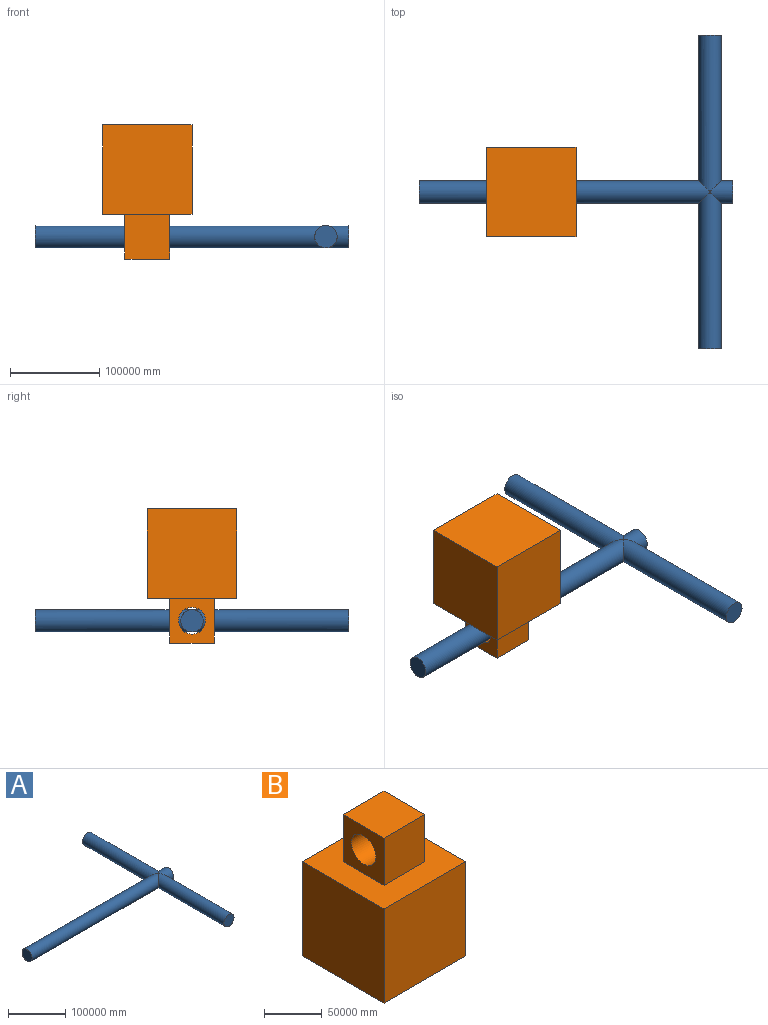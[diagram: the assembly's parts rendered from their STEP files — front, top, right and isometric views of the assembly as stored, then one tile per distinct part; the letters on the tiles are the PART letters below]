
ASSEMBLY  parts=2 mates=1
PART A: 6 faces, bbox 350000x350000x25038.9 mm
  f0: cylinder r=12500mm len=350000mm, axis (0,-1,0), area 26239011832.4mm2, adj f1,f2,f3
  f1: plane 25000x25000mm, normal (0,1,0), area 490873852.1mm2, adj f0
  f2: plane 25000x25000mm, normal (0,-1,0), area 490873852.1mm2, adj f0
  f3: cylinder r=12500mm len=350000mm, axis (-1,0,0), area 26239045544.5mm2, adj f0,f4,f5
  f4: plane 25000x25000mm, normal (1,0,0), area 490873852.1mm2, adj f3
  f5: plane 25000x25000mm, normal (-1,0,0), area 490873852.1mm2, adj f3
PART B: 12 faces, bbox 100000x100000x150000 mm
  f0: plane 100000x100000mm, normal (0,0,1), area 7500000000mm2, adj f1,f2,f3,f4,f6,f7,f8,f9
  f1: plane 100000x100000mm, normal (0,1,0), area 10000000000mm2, adj f0,f2,f4,f5
  f2: plane 100000x100000mm, normal (-1,0,0), area 10000000000mm2, adj f0,f1,f3,f5
  f3: plane 100000x100000mm, normal (0,-1,0), area 10000000000mm2, adj f0,f2,f4,f5
  f4: plane 100000x100000mm, normal (1,0,0), area 10000000000mm2, adj f0,f1,f3,f5
  f5: plane 100000x100000mm, normal (0,0,-1), area 10000000000mm2, adj f1,f2,f3,f4
  f6: plane 50000x50000mm, normal (1,0,0), area 1793141652.9mm2, adj f0,f7,f9,f10,f11
  f7: plane 50000x50000mm, normal (0,1,0), area 2500000000mm2, adj f0,f6,f8,f10
  f8: plane 50000x50000mm, normal (-1,0,0), area 1793141652.9mm2, adj f0,f7,f9,f10,f11
  f9: plane 50000x50000mm, normal (0,-1,0), area 2500000000mm2, adj f0,f6,f8,f10
  f10: plane 50000x50000mm, normal (0,0,1), area 2500000000mm2, adj f6,f7,f8,f9
  f11: cylinder r=15000mm len=50000mm, axis (1,0,0), area 4712388980.4mm2, adj f6,f8
PLACE A at identity
PLACE B rot(axis=(0,1,0),180deg) t=(-25000,0,250000)mm fixed
MATE revolute B.f11 <-> A.f3  axis (1,0,0) through (0,0,125000)mm
